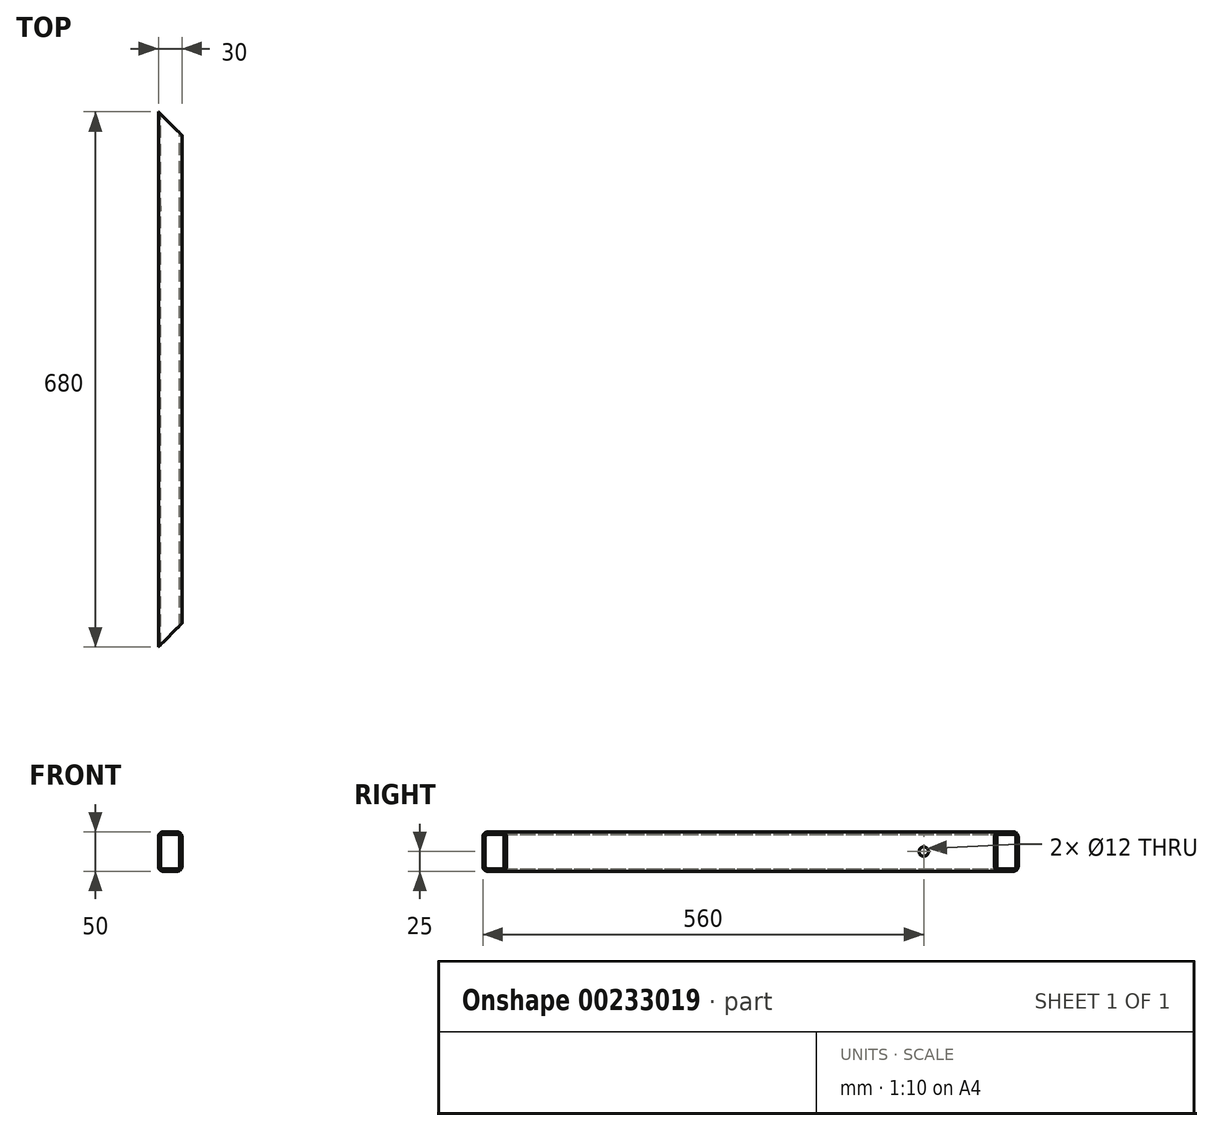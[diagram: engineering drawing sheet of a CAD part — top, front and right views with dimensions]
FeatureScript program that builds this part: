
annotation { "Feature Type Name" : "Feature", "Feature Type Description" : "" }
export const myFeature = defineFeature(function(context is Context, id is Id, definition is map)
    precondition{}
    {
        {
            var Q0;
            Q0=qCreatedBy(makeId("Front.planeOp"),FACE);
            var sketch = newSketch(context, id + "F0", { "sketchPlane" : qUnion([Q0])});
            skLineSegment(sketch, "E0.bottom", {"start": v(9, 25) * mm, "end": v(-9, 25) * mm});
            skLineSegment(sketch, "E0.top", {"start": v(9, -25) * mm, "end": v(-9, -25) * mm});
            skLineSegment(sketch, "E0.left", {"start": v(15, 19) * mm, "end": v(15, -19) * mm});
            skLineSegment(sketch, "E0.right", {"start": v(-15, 19) * mm, "end": v(-15, -19) * mm});
            skPoint(sketch, "E0.middle", {"position": v(0, 0) * mm});
            skPoint(sketch, "E1.visualSharp", {"position": v(-15, 25) * mm});
            skArc(sketch, "E1.filletArc", {"start": v(-9, 25) * mm, "mid": v(-13.24, 23.24) * mm, "end": v(-15, 19) * mm});
            skPoint(sketch, "E2.visualSharp", {"position": v(-15, -25) * mm});
            skArc(sketch, "E2.filletArc", {"start": v(-15, -19) * mm, "mid": v(-13.24, -23.24) * mm, "end": v(-9, -25) * mm});
            skPoint(sketch, "E3.visualSharp", {"position": v(15, -25) * mm});
            skArc(sketch, "E3.filletArc", {"start": v(9, -25) * mm, "mid": v(13.24, -23.24) * mm, "end": v(15, -19) * mm});
            skPoint(sketch, "E4.visualSharp", {"position": v(15, 25) * mm});
            skArc(sketch, "E4.filletArc", {"start": v(15, 19) * mm, "mid": v(13.24, 23.24) * mm, "end": v(9, 25) * mm});
            skLineSegment(sketch, "E5.0", {"start": v(9, 22) * mm, "end": v(-9, 22) * mm});
            skArc(sketch, "E5.1", {"start": v(12, 19) * mm, "mid": v(11.12, 21.12) * mm, "end": v(9, 22) * mm});
            skArc(sketch, "E5.2", {"start": v(-9, 22) * mm, "mid": v(-11.12, 21.12) * mm, "end": v(-12, 19) * mm});
            skLineSegment(sketch, "E5.3", {"start": v(12, 19) * mm, "end": v(12, -19) * mm});
            skLineSegment(sketch, "E5.4", {"start": v(-12, 19) * mm, "end": v(-12, -19) * mm});
            skArc(sketch, "E5.5", {"start": v(-12, -19) * mm, "mid": v(-11.12, -21.12) * mm, "end": v(-9, -22) * mm});
            skLineSegment(sketch, "E5.6", {"start": v(9, -22) * mm, "end": v(-9, -22) * mm});
            skArc(sketch, "E5.7", {"start": v(9, -22) * mm, "mid": v(11.12, -21.12) * mm, "end": v(12, -19) * mm});
            skSolve(sketch);
        }
        {
            var Q0;
            Q0=makeQuery(id+"F0.imprint","IMPRINT",FACE,{"disambiguationData":[TD([[makeQuery(id+"F0.imprint","IMPRINT",EDGE,{"derivedFrom":sQuery(id+"F0.wireOp",EDGE,"E0.bottom")}),1.0]])]});
            extrude(context, id + "F1", {"entities" : qUnion([Q0]), "endBound" : BoundingType.SYMMETRIC, "depth" : 680 * mm});
        }
        {
            var Q0;
            Q0=makeQuery(id+"F1.opExtrude","SWEPT_FACE",FACE,{"disambiguationData":[OSD([sQuery(id+"F0.wireOp",EDGE,"E0.bottom")])]});
            var sketch = newSketch(context, id + "F2", { "sketchPlane" : qUnion([Q0])});
            skLineSegment(sketch, "E6.left", {"start": v(15, 310) * mm, "end": v(15, 340) * mm});
            skPoint(sketch, "E6.middle", {"position": v(0, 340) * mm});
            skLineSegment(sketch, "E7", {"start": v(15, 310) * mm, "end": v(-15, 340) * mm});
            skLineSegment(sketch, "E8", {"start": v(-15, 340) * mm, "end": v(15, 340) * mm});
            skPoint(sketch, "E8.endSnap0", {"position": v(15, 340) * mm});
            skPoint(sketch, "E9.orphan", {"position": v(17.67, 340) * mm});
            skPoint(sketch, "E6.top.end.orphan", {"position": v(-15, 370) * mm});
            skPoint(sketch, "E6.top.start.orphan", {"position": v(15, 370) * mm});
            skPoint(sketch, "E6.right.start.orphan", {"position": v(-15, 310) * mm});
            skLineSegment(sketch, "E10.MirrorCS", {"start": v(-15, -340) * mm, "end": v(15, -340) * mm});
            skPoint(sketch, "E11.MirrorP", {"position": v(17.67, -340) * mm});
            skPoint(sketch, "E12.MirrorP", {"position": v(-15, -310) * mm});
            skLineSegment(sketch, "E13.MirrorCS", {"start": v(15, -310) * mm, "end": v(15, -340) * mm});
            skLineSegment(sketch, "E14.MirrorCS", {"start": v(15, -310) * mm, "end": v(-15, -340) * mm});
            skPoint(sketch, "E15.MirrorP", {"position": v(15, -340) * mm});
            skPoint(sketch, "E16.MirrorP", {"position": v(0, -340) * mm});
            skSolve(sketch);
        }
        {
            var Q0;
            {var subQ0=sQuery(id+"F2.wireOp",EDGE,"E10.MirrorCS");var subQ1=makeQuery(id+"F1.opExtrude","SWEPT_EDGE",EDGE,{"disambiguationData":[OSD([sQuery(id+"F0.wireOp",EDGE,"E0.bottom"),sQuery(id+"F0.wireOp",EDGE,"E1.filletArc")])]});var subQ2=makeQuery(id+"F2.imprint","INTERSECT",VERTEX,{"derivedFrom":[subQ1,subQ0]});var subQ3=sQuery(id+"F2.wireOp",EDGE,"E14.MirrorCS");var subQ4=makeQuery(id+"F2.imprint","INTERSECT",VERTEX,{"derivedFrom":[subQ0,subQ3]});Q0=makeQuery(id+"F2.imprint","IMPRINT",FACE,{"disambiguationData":[TD([[makeQuery(id+"F2.imprint","IMPRINT",EDGE,{"disambiguationData":[TD([[subQ2,1.0],[subQ4,-1.0]])],"derivedFrom":subQ0}),1.0]])]});}
            var Q1;
            {var subQ0=sQuery(id+"F2.wireOp",EDGE,"E10.MirrorCS");var subQ1=sQuery(id+"F0.wireOp",EDGE,"E0.bottom");var subQ2=makeQuery(id+"F1.opExtrude","SWEPT_EDGE",EDGE,{"disambiguationData":[OSD([subQ1,sQuery(id+"F0.wireOp",EDGE,"E4.filletArc")])]});var subQ3=makeQuery(id+"F2.imprint","INTERSECT",VERTEX,{"derivedFrom":[subQ2,subQ0]});var subQ4=makeQuery(id+"F1.opExtrude","SWEPT_EDGE",EDGE,{"disambiguationData":[OSD([subQ1,sQuery(id+"F0.wireOp",EDGE,"E1.filletArc")])]});var subQ5=makeQuery(id+"F2.imprint","INTERSECT",VERTEX,{"derivedFrom":[subQ4,subQ0]});Q1=makeQuery(id+"F2.imprint","IMPRINT",FACE,{"disambiguationData":[TD([[makeQuery(id+"F2.imprint","IMPRINT",EDGE,{"disambiguationData":[TD([[subQ3,-1.0],[subQ5,1.0]])],"derivedFrom":subQ0}),-1.0]])]});}
            var Q2;
            {var subQ3=sQuery(id+"F2.wireOp",EDGE,"E13.MirrorCS");Q2=makeQuery(id+"F2.imprint","IMPRINT",FACE,{"disambiguationData":[TD([[makeQuery(id+"F2.imprint","IMPRINT",EDGE,{"derivedFrom":subQ3}),-1.0]])]});}
            var Q3;
            {var subQ0=sQuery(id+"F2.wireOp",EDGE,"E8");var subQ1=sQuery(id+"F2.wireOp",EDGE,"E7");var subQ2=makeQuery(id+"F2.imprint","INTERSECT",VERTEX,{"derivedFrom":[subQ1,subQ0]});Q3=makeQuery(id+"F2.imprint","IMPRINT",FACE,{"disambiguationData":[TD([[makeQuery(id+"F2.imprint","IMPRINT",EDGE,{"disambiguationData":[TD([[subQ2,1.0]])],"derivedFrom":subQ1}),-1.0]])]});}
            var Q4;
            {var subQ0=sQuery(id+"F2.wireOp",EDGE,"E7");var subQ1=sQuery(id+"F0.wireOp",EDGE,"E0.bottom");var subQ2=makeQuery(id+"F1.opExtrude","SWEPT_EDGE",EDGE,{"disambiguationData":[OSD([subQ1,sQuery(id+"F0.wireOp",EDGE,"E4.filletArc")])]});var subQ3=makeQuery(id+"F2.imprint","INTERSECT",VERTEX,{"derivedFrom":[subQ2,subQ0]});Q4=makeQuery(id+"F2.imprint","IMPRINT",FACE,{"disambiguationData":[TD([[makeQuery(id+"F2.imprint","IMPRINT",EDGE,{"disambiguationData":[TD([[subQ3,-1.0]])],"derivedFrom":subQ0}),-1.0]])]});}
            var Q5;
            {var subQ0=sQuery(id+"F2.wireOp",EDGE,"E6.left");Q5=makeQuery(id+"F2.imprint","IMPRINT",FACE,{"disambiguationData":[TD([[makeQuery(id+"F2.imprint","IMPRINT",EDGE,{"derivedFrom":subQ0}),1.0]])]});}
            var Q6;
            Q6=makeQuery(id+"F1.opExtrude","SWEPT_FACE",FACE,{"disambiguationData":[OSD([sQuery(id+"F0.wireOp",EDGE,"E0.top")])]});
            extrude(context, id + "F3", {"entities" : qUnion([Q0, Q1, Q2, Q3, Q4, Q5]), "operationType" : NewBodyOperationType.REMOVE, "endBound" : BoundingType.UP_TO_SURFACE, "oppositeDirection" : true, "endBoundEntityFace" : qUnion([Q6]), "depth" : 25 * mm});
        }
        {
            var Q0;
            Q0=makeQuery(id+"F1.opExtrude","SWEPT_FACE",FACE,{"disambiguationData":[OSD([sQuery(id+"F0.wireOp",EDGE,"E0.right")])]});
            var sketch = newSketch(context, id + "F4", { "sketchPlane" : qUnion([Q0])});
            skPoint(sketch, "E17", {"position": v(-220, 0) * mm});
            skSolve(sketch);
        }
        {
            var Q0;
            Q0=sQuery(id+"F4.wireOp",VERTEX,"E17");
            var Q1;
            Q1=makeQuery(id+"F1.opExtrude","SWEPT_BODY",BODY,{"disambiguationData":[OSD([sQuery(id+"F0.wireOp",EDGE,"E0.bottom"),sQuery(id+"F0.wireOp",EDGE,"E0.top"),sQuery(id+"F0.wireOp",EDGE,"E0.left"),sQuery(id+"F0.wireOp",EDGE,"E0.right"),sQuery(id+"F0.wireOp",EDGE,"E1.filletArc"),sQuery(id+"F0.wireOp",EDGE,"E2.filletArc"),sQuery(id+"F0.wireOp",EDGE,"E3.filletArc"),sQuery(id+"F0.wireOp",EDGE,"E4.filletArc"),sQuery(id+"F0.wireOp",EDGE,"E5.0"),sQuery(id+"F0.wireOp",EDGE,"E5.1"),sQuery(id+"F0.wireOp",EDGE,"E5.2"),sQuery(id+"F0.wireOp",EDGE,"E5.3"),sQuery(id+"F0.wireOp",EDGE,"E5.4"),sQuery(id+"F0.wireOp",EDGE,"E5.5"),sQuery(id+"F0.wireOp",EDGE,"E5.6"),sQuery(id+"F0.wireOp",EDGE,"E5.7")])]});
            hole(context, id + "F5", {"style" : HoleStyle.SIMPLE, "endStyle" : HoleEndStyle.THROUGH, "holeDiameter" : 12 * mm, "startFromSketch" : true, "locations" : qUnion([Q0]), "scope" : qUnion([Q1]), "isTappedThrough" : true});
        }
    });
